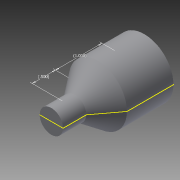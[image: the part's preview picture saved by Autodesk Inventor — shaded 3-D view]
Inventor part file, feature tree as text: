
AUTODESK INVENTOR PART (.ipt)
format: ipt  version: 2014 SP1 (Build 180222100, 222)  size: 160,256 bytes
history: native  units: in
note: dims shown in document units (in); Inventor stores cm internally (conversion verified against a paired STEP export)
features: sketch x4, extrude x4, projected_geometry x2, pattern_circular x1, revolve x1
ambient origin geometry x8: Origin, YZ Plane, XZ Plane, XY Plane, X Axis, Y Axis, Z Axis, Center Point
bodies: Solid1 (feature_tree)
feature tree (12):
  sketch  "Sketch1"  dims[d0=1.25in d2=60.0deg d3=0.1575in d4=0.7874in]
  extrude  "Extrusion1"  Depth=0.1575in TaperAngle=60.0deg
  extrude  "Extrusion2"  Depth=2.3622in TaperAngle=360.0deg
  extrude  "Extrusion3"  Depth=0.6in TaperAngle=0.0deg
  pattern_circular  "Circular Pattern1"  Count=6 Angle=360.0deg
  extrude  "Extrusion4"  Depth=0.25in
  revolve  "Revolution1"  [1 undecoded]
  sketch  "Sketch5"  dims[d14=0.6in d15=0.0in d16=2.3622in d17=360.0deg d19=0.375in d20=0.3in d21=0.0in d22=1.0in d23=0.25in d24=0.5in d25=90.0deg d26=1.0in d27=0.5in]
  sketch  "Sketch2"  dims[d5=0.6378in d6=2.3622in d8=360.0deg]
  sketch  "Sketch4"  dims[d10=1.0in d11=0.0in d12=0.6in d13=0.0in]
  projected_geometry  "Project Cut Edges1"
  projected_geometry  "Project Cut Edges2"
note: 1 required parameter value undecoded (feature->parameter linkage not recoverable at this tier; creation-order binding heuristic only, values carry confidence <= 0.55)
